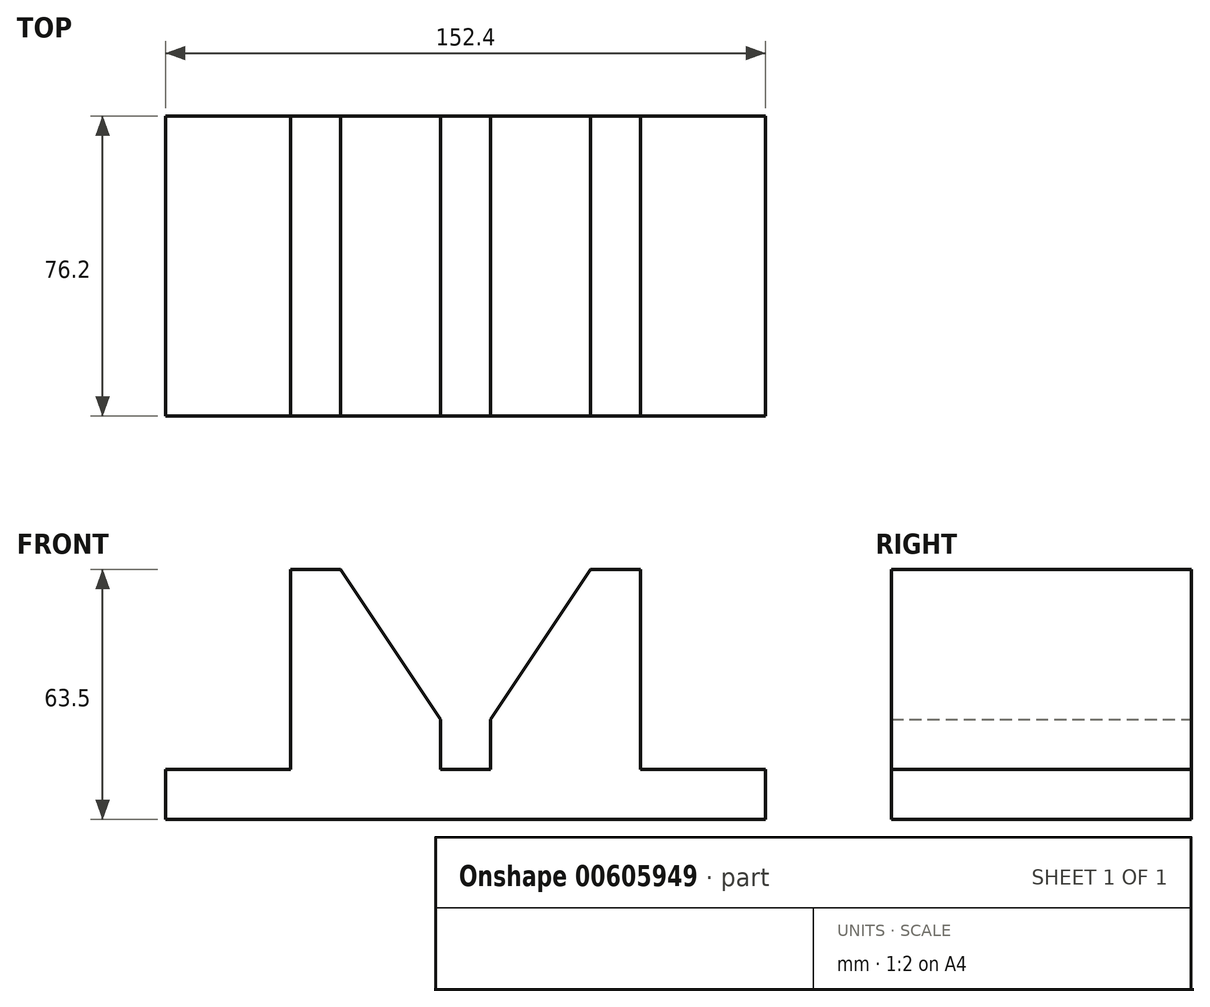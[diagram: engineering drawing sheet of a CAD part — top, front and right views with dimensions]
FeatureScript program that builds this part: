
annotation { "Feature Type Name" : "Feature", "Feature Type Description" : "" }
export const myFeature = defineFeature(function(context is Context, id is Id, definition is map)
    precondition{}
    {
        {
            var Q0;
            Q0=qCreatedBy(makeId("Front.planeOp"),FACE);
            var sketch = newSketch(context, id + "F0", { "sketchPlane" : qUnion([Q0])});
            skLineSegment(sketch, "E0", {"start": v(0, 0) * mm, "end": v(152.4, 0) * mm});
            skLineSegment(sketch, "E1", {"start": v(0, 0) * mm, "end": v(0, 12.7) * mm});
            skLineSegment(sketch, "E2", {"start": v(0, 12.7) * mm, "end": v(31.75, 12.7) * mm});
            skLineSegment(sketch, "E3", {"start": v(31.75, 12.7) * mm, "end": v(31.75, 63.5) * mm});
            skLineSegment(sketch, "E4", {"start": v(31.75, 63.5) * mm, "end": v(44.45, 63.5) * mm});
            skLineSegment(sketch, "E5", {"start": v(76.2, 12.7) * mm, "end": v(82.55, 12.7) * mm});
            skLineSegment(sketch, "E6", {"start": v(76.2, 12.7) * mm, "end": v(69.85, 12.7) * mm});
            skLineSegment(sketch, "E7", {"start": v(69.85, 12.7) * mm, "end": v(69.85, 25.4) * mm});
            skLineSegment(sketch, "E8", {"start": v(69.85, 25.4) * mm, "end": v(44.45, 63.5) * mm});
            skLineSegment(sketch, "E9", {"start": v(82.55, 12.7) * mm, "end": v(82.55, 25.4) * mm});
            skLineSegment(sketch, "E10", {"start": v(152.4, 0) * mm, "end": v(152.4, 12.7) * mm});
            skLineSegment(sketch, "E11", {"start": v(152.4, 12.7) * mm, "end": v(120.65, 12.7) * mm});
            skLineSegment(sketch, "E12", {"start": v(120.65, 12.7) * mm, "end": v(120.65, 63.5) * mm});
            skLineSegment(sketch, "E13", {"start": v(120.65, 63.5) * mm, "end": v(107.95, 63.5) * mm});
            skLineSegment(sketch, "E14", {"start": v(107.95, 63.5) * mm, "end": v(82.55, 25.4) * mm});
            skSolve(sketch);
        }
        {
            var Q0;
            Q0=makeQuery(id+"F0.imprint","IMPRINT",FACE,{"disambiguationData":[TD([[makeQuery(id+"F0.imprint","IMPRINT",EDGE,{"derivedFrom":sQuery(id+"F0.wireOp",EDGE,"E0")}),1.0]])]});
            extrude(context, id + "F1", {"entities" : qUnion([Q0]), "depth" : 76.2 * mm, "offsetDistance" : 25.4 * mm});
        }
    });
